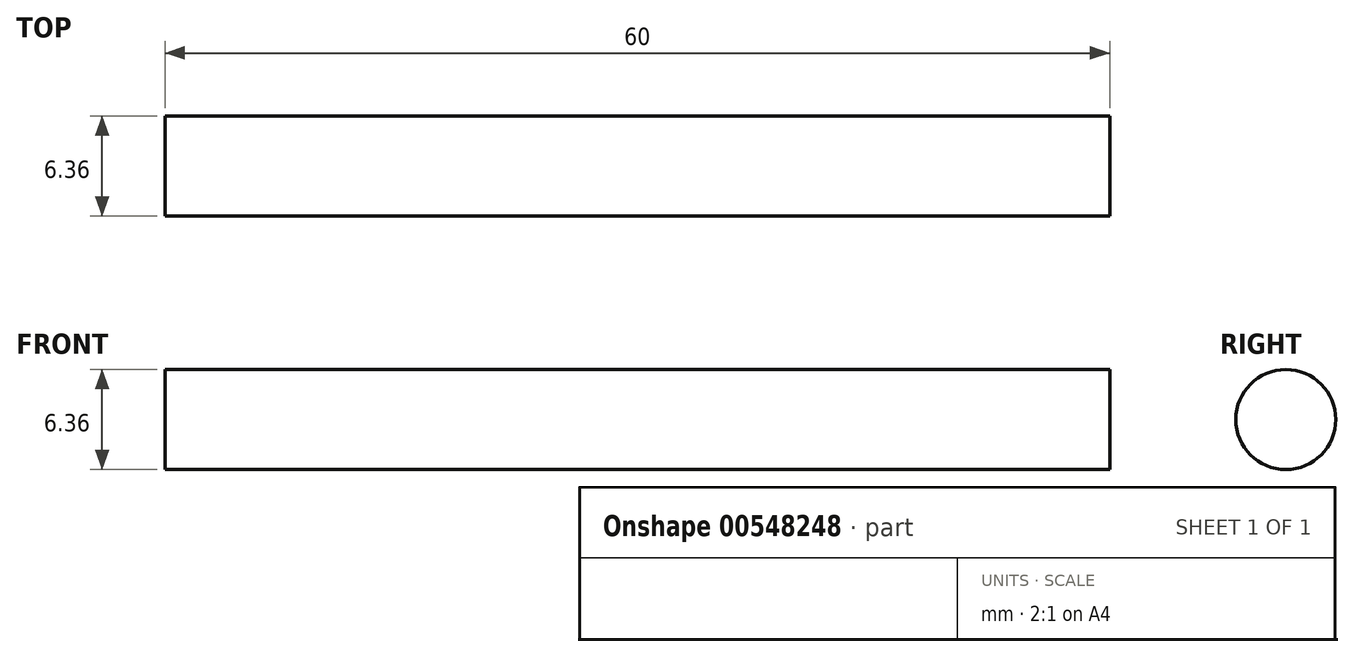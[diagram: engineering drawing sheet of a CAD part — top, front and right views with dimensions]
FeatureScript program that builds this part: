
annotation { "Feature Type Name" : "Feature", "Feature Type Description" : "" }
export const myFeature = defineFeature(function(context is Context, id is Id, definition is map)
    precondition{}
    {
        {
            var Q0;
            Q0=qCreatedBy(makeId("Right.planeOp"),FACE);
            var sketch = newSketch(context, id + "F0", { "sketchPlane" : qUnion([Q0])});
            skCircle(sketch, "E0", {"center": v(0, 0) * mm, "radius": 3.18 * mm});
            skSolve(sketch);
        }
        {
            var Q0;
            Q0=makeQuery(id+"F0.imprint","IMPRINT",FACE,{"disambiguationData":[TD([[makeQuery(id+"F0.imprint","IMPRINT",EDGE,{"derivedFrom":sQuery(id+"F0.wireOp",EDGE,"E0")}),1.0]])]});
            extrude(context, id + "F1", {"entities" : qUnion([Q0]), "endBound" : BoundingType.SYMMETRIC, "depth" : 60 * mm, "offsetDistance" : 25 * mm});
        }
    });
